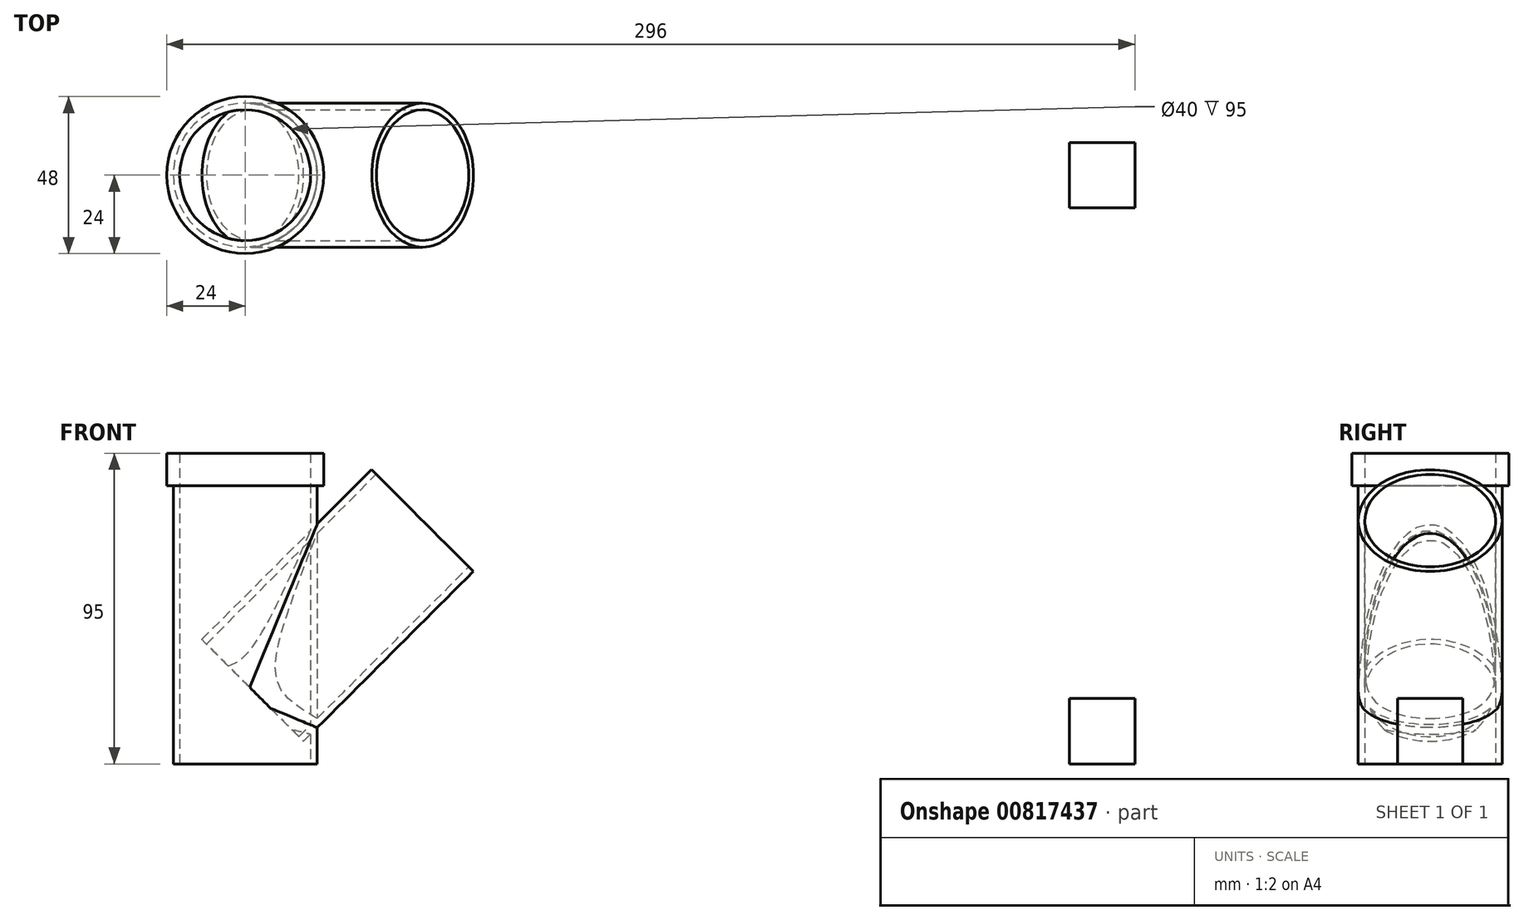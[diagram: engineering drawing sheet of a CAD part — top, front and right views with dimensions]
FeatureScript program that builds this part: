
annotation { "Feature Type Name" : "Feature", "Feature Type Description" : "" }
export const myFeature = defineFeature(function(context is Context, id is Id, definition is map)
    precondition{}
    {
        {
            var Q0;
            Q0=qCreatedBy(makeId("Front.planeOp"),FACE);
            var sketch = newSketch(context, id + "F0", { "sketchPlane" : qUnion([Q0])});
            skLineSegment(sketch, "E0.bottom", {"start": v(0, -45.5) * mm, "end": v(20, -45.5) * mm, "construction": true});
            skLineSegment(sketch, "E0.top", {"start": v(0, 45.5) * mm, "end": v(20, 45.5) * mm, "construction": true});
            skLineSegment(sketch, "E0.right", {"start": v(20, -45.5) * mm, "end": v(20, 45.5) * mm});
            skLineSegment(sketch, "E1.bottom", {"start": v(0, -47.5) * mm, "end": v(20, -47.5) * mm, "construction": true});
            skLineSegment(sketch, "E1.top", {"start": v(0, 47.5) * mm, "end": v(20, 47.5) * mm, "construction": true});
            skLineSegment(sketch, "E1.left", {"start": v(0, -47.5) * mm, "end": v(0, -45.5) * mm});
            skLineSegment(sketch, "E1.right", {"start": v(22, -47.5) * mm, "end": v(22, 47.5) * mm});
            skLineSegment(sketch, "E2.bottom", {"start": v(22, 37.5) * mm, "end": v(24, 37.5) * mm});
            skLineSegment(sketch, "E2.top", {"start": v(22, 47.5) * mm, "end": v(24, 47.5) * mm});
            skLineSegment(sketch, "E2.left", {"start": v(22, 37.5) * mm, "end": v(22, 47.5) * mm});
            skLineSegment(sketch, "E2.right", {"start": v(24, 37.5) * mm, "end": v(24, 47.5) * mm});
            skLineSegment(sketch, "E3.trimOffspring", {"start": v(0, 45.5) * mm, "end": v(0, 47.5) * mm});
            skLineSegment(sketch, "E4", {"start": v(0, -45.5) * mm, "end": v(0, 45.5) * mm, "construction": true});
            skLineSegment(sketch, "E5", {"start": v(20, 45.5) * mm, "end": v(20, 47.5) * mm});
            skLineSegment(sketch, "E6", {"start": v(20, -45.5) * mm, "end": v(20, -47.5) * mm});
            skLineSegment(sketch, "E7", {"start": v(20, -47.5) * mm, "end": v(22, -47.5) * mm});
            skLineSegment(sketch, "E8", {"start": v(20, 47.5) * mm, "end": v(22, 47.5) * mm});
            skLineSegment(sketch, "E9", {"start": v(54.2, 26.9) * mm, "end": v(38.64, 42.46) * mm, "construction": true});
            skLineSegment(sketch, "E10", {"start": v(38.64, 42.46) * mm, "end": v(0, 3.82) * mm});
            skLineSegment(sketch, "E11", {"start": v(40.05, 41.05) * mm, "end": v(0, 1) * mm});
            skLineSegment(sketch, "E12", {"start": v(38.64, 42.46) * mm, "end": v(40.05, 41.05) * mm});
            skLineSegment(sketch, "E13", {"start": v(0, 3.82) * mm, "end": v(0, 1) * mm});
            skLineSegment(sketch, "E14", {"start": v(0, 3.82) * mm, "end": v(-13.28, -9.45) * mm});
            skLineSegment(sketch, "E15", {"start": v(-13.28, -9.45) * mm, "end": v(-11.86, -10.87) * mm});
            skLineSegment(sketch, "E16", {"start": v(0, 1) * mm, "end": v(-11.86, -10.87) * mm});
            skLineSegment(sketch, "E17", {"start": v(54.2, 26.9) * mm, "end": v(0, -27.29) * mm, "construction": true});
            skLineSegment(sketch, "E18", {"start": v(22, -47.5) * mm, "end": v(272, -47.5) * mm, "construction": true});
            skLineSegment(sketch, "E19.bottom", {"start": v(272, -47.5) * mm, "end": v(252, -47.5) * mm});
            skLineSegment(sketch, "E19.top", {"start": v(272, -27.5) * mm, "end": v(252, -27.5) * mm});
            skLineSegment(sketch, "E19.left", {"start": v(272, -47.5) * mm, "end": v(272, -27.5) * mm});
            skLineSegment(sketch, "E19.right", {"start": v(252, -47.5) * mm, "end": v(252, -27.5) * mm});
            skSolve(sketch);
        }
        {
            var Q0;
            {var subQ0=sQuery(id+"F0.wireOp",EDGE,"E2.bottom");Q0=makeQuery(id+"F0.imprint","IMPRINT",FACE,{"disambiguationData":[TD([[makeQuery(id+"F0.imprint","IMPRINT",EDGE,{"derivedFrom":subQ0}),1.0]])]});}
            var Q1;
            {var subQ0=sQuery(id+"F0.wireOp",EDGE,"E5");Q1=makeQuery(id+"F0.imprint","IMPRINT",FACE,{"disambiguationData":[TD([[makeQuery(id+"F0.imprint","IMPRINT",EDGE,{"derivedFrom":subQ0}),-1.0]])]});}
            var Q2;
            {var subQ1=sQuery(id+"F0.wireOp",EDGE,"E6");Q2=makeQuery(id+"F0.imprint","IMPRINT",FACE,{"disambiguationData":[TD([[makeQuery(id+"F0.imprint","IMPRINT",EDGE,{"derivedFrom":subQ1}),1.0]])]});}
            var Q3;
            {var subQ0=sQuery(id+"F0.wireOp",EDGE,"E2.bottom");Q3=makeQuery(id+"F0.imprint","IMPRINT",FACE,{"disambiguationData":[TD([[makeQuery(id+"F0.imprint","IMPRINT",EDGE,{"derivedFrom":subQ0}),1.0]])]});}
            var Q4;
            {var subQ0=sQuery(id+"F0.wireOp",EDGE,"E10");var subQ1=sQuery(id+"F0.wireOp",EDGE,"E0.right");var subQ2=makeQuery(id+"F0.imprint","INTERSECT",VERTEX,{"derivedFrom":[subQ1,subQ0]});Q4=makeQuery(id+"F0.imprint","IMPRINT",FACE,{"disambiguationData":[TD([[makeQuery(id+"F0.imprint","IMPRINT",EDGE,{"disambiguationData":[TD([[subQ2,1.0]])],"derivedFrom":subQ1}),-1.0]])]});}
            var Q5;
            Q5=sQuery(id+"F0.wireOp",EDGE,"E1.left");
            revolve(context, id + "F1", {"surfaceOperationType" : NewSurfaceOperationType.NEW, "entities" : qUnion([Q0, Q1, Q2, Q3, Q4]), "axis" : qUnion([Q5]), "revolveType" : RevolveType.FULL});
        }
        {
            var Q0;
            {var subQ5=sQuery(id+"F0.wireOp",EDGE,"E12");Q0=makeQuery(id+"F0.imprint","IMPRINT",FACE,{"disambiguationData":[TD([[makeQuery(id+"F0.imprint","IMPRINT",EDGE,{"derivedFrom":subQ5}),-1.0]])]});}
            var Q1;
            {var subQ5=sQuery(id+"F0.wireOp",EDGE,"E13");Q1=makeQuery(id+"F0.imprint","IMPRINT",FACE,{"disambiguationData":[TD([[makeQuery(id+"F0.imprint","IMPRINT",EDGE,{"derivedFrom":subQ5}),1.0]])]});}
            var Q2;
            Q2=makeQuery(id+"F0.imprint","IMPRINT",FACE,{"disambiguationData":[TD([[makeQuery(id+"F0.imprint","IMPRINT",EDGE,{"derivedFrom":sQuery(id+"F0.wireOp",EDGE,"E13")}),-1.0]])]});
            var Q3;
            {var subQ0=sQuery(id+"F0.wireOp",EDGE,"E10");var subQ1=sQuery(id+"F0.wireOp",EDGE,"E0.right");var subQ2=makeQuery(id+"F0.imprint","INTERSECT",VERTEX,{"derivedFrom":[subQ1,subQ0]});Q3=makeQuery(id+"F0.imprint","IMPRINT",FACE,{"disambiguationData":[TD([[makeQuery(id+"F0.imprint","IMPRINT",EDGE,{"disambiguationData":[TD([[subQ2,1.0]])],"derivedFrom":subQ1}),-1.0]])]});}
            var Q4;
            Q4=sQuery(id+"F0.wireOp",EDGE,"E17");
            revolve(context, id + "F2", {"operationType" : NewBodyOperationType.ADD, "surfaceOperationType" : NewSurfaceOperationType.NEW, "entities" : qUnion([Q0, Q1, Q2, Q3]), "axis" : qUnion([Q4]), "revolveType" : RevolveType.FULL});
        }
        {
            var Q0;
            {var subQ0=sQuery(id+"F0.wireOp",EDGE,"E2.bottom");var subQ6=sQuery(id+"F0.wireOp",EDGE,"E5");var subQ7=sQuery(id+"F0.wireOp",EDGE,"E10");var subQ8=sQuery(id+"F0.wireOp",EDGE,"E0.right");var subQ9=makeQuery(id+"F0.imprint","INTERSECT",VERTEX,{"derivedFrom":[subQ8,subQ7]});var subQ13=sQuery(id+"F0.wireOp",EDGE,"E6");var subQ18=makeQuery(id+"F0.imprint","IMPRINT",EDGE,{"disambiguationData":[TD([[subQ9,1.0]])],"derivedFrom":subQ8});var subQ20=sQuery(id+"F0.wireOp",EDGE,"E13");var subQ21=makeQuery(id+"F0.imprint","IMPRINT",EDGE,{"derivedFrom":subQ20});var subQ24=sQuery(id+"F0.wireOp",EDGE,"E12");Q0=qUnion([makeQuery(id+"F0.imprint","IMPRINT",FACE,{"disambiguationData":[TD([[makeQuery(id+"F0.imprint","IMPRINT",EDGE,{"derivedFrom":sQuery(id+"F0.wireOp",EDGE,"E19.bottom")}),-1.0]])]}),makeQuery(id+"F0.imprint","IMPRINT",FACE,{"disambiguationData":[TD([[makeQuery(id+"F0.imprint","IMPRINT",EDGE,{"derivedFrom":subQ24}),-1.0]])]}),makeQuery(id+"F0.imprint","IMPRINT",FACE,{"disambiguationData":[TD([[subQ21,1.0]])]}),makeQuery(id+"F0.imprint","IMPRINT",FACE,{"disambiguationData":[TD([[subQ21,-1.0]])]}),makeQuery(id+"F0.imprint","IMPRINT",FACE,{"disambiguationData":[TD([[subQ18,-1.0]])]}),makeQuery(id+"F0.imprint","IMPRINT",FACE,{"disambiguationData":[TD([[makeQuery(id+"F0.imprint","IMPRINT",EDGE,{"derivedFrom":subQ13}),1.0]])]}),makeQuery(id+"F0.imprint","IMPRINT",FACE,{"disambiguationData":[TD([[makeQuery(id+"F0.imprint","IMPRINT",EDGE,{"derivedFrom":subQ6}),-1.0]])]}),makeQuery(id+"F0.imprint","IMPRINT",FACE,{"disambiguationData":[TD([[makeQuery(id+"F0.imprint","IMPRINT",EDGE,{"derivedFrom":subQ0}),1.0]])]})]);}
            var Q1;
            Q1=makeQuery(id+"F0.imprint","IMPRINT",FACE,{"disambiguationData":[TD([[makeQuery(id+"F0.imprint","IMPRINT",EDGE,{"derivedFrom":sQuery(id+"F0.wireOp",EDGE,"E19.bottom")}),-1.0]])]});
            extrude(context, id + "F3", {"entities" : qUnion([Q0, Q1]), "endBound" : BoundingType.SYMMETRIC, "depth" : 20 * mm, "offsetDistance" : 25 * mm});
        }
        {
            var Q0;
            Q0=makeQuery(id+"F3.opExtrude","SWEPT_BODY",BODY,{"disambiguationData":[OSD([sQuery(id+"F0.wireOp",EDGE,"E0.right"),sQuery(id+"F0.wireOp",EDGE,"E1.right"),sQuery(id+"F0.wireOp",EDGE,"E2.bottom"),sQuery(id+"F0.wireOp",EDGE,"E2.top"),sQuery(id+"F0.wireOp",EDGE,"E2.right"),sQuery(id+"F0.wireOp",EDGE,"E5"),sQuery(id+"F0.wireOp",EDGE,"E6"),sQuery(id+"F0.wireOp",EDGE,"E7"),sQuery(id+"F0.wireOp",EDGE,"E8"),sQuery(id+"F0.wireOp",EDGE,"E10"),sQuery(id+"F0.wireOp",EDGE,"E11"),sQuery(id+"F0.wireOp",EDGE,"E12"),sQuery(id+"F0.wireOp",EDGE,"E14"),sQuery(id+"F0.wireOp",EDGE,"E15"),sQuery(id+"F0.wireOp",EDGE,"E16")])]});
            deleteBodies(context, id + "F4", {"entities" : qUnion([Q0])});
        }
    });
